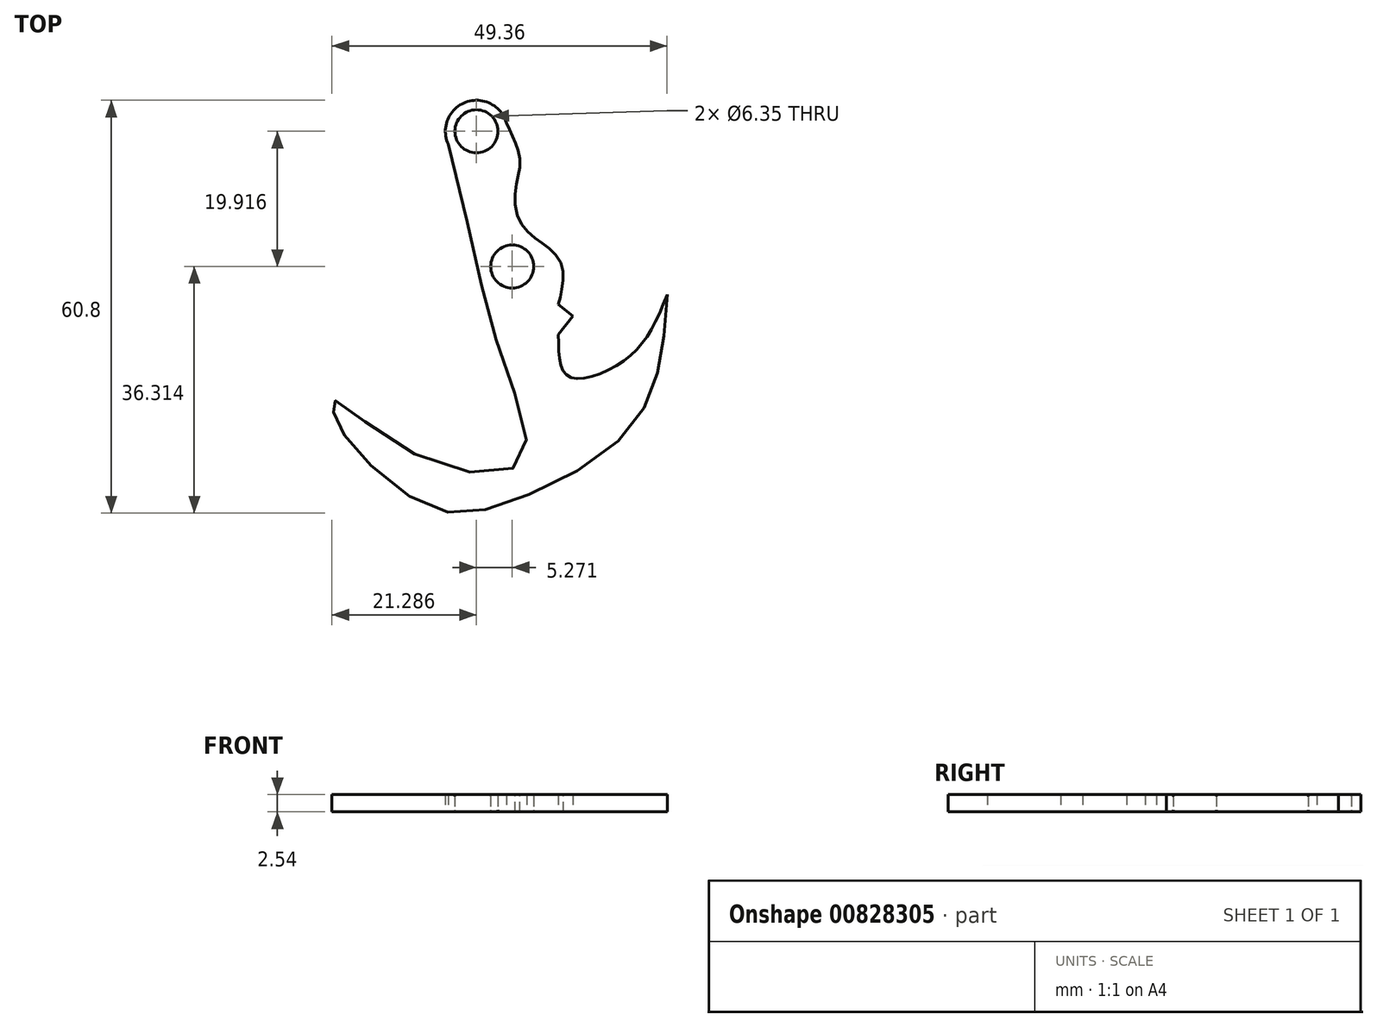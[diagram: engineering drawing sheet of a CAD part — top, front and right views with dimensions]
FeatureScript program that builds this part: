
annotation { "Feature Type Name" : "Feature", "Feature Type Description" : "" }
export const myFeature = defineFeature(function(context is Context, id is Id, definition is map)
    precondition{}
    {
        {
            var Q0;
            Q0=qCreatedBy(makeId("Top.planeOp"),FACE);
            var sketch = newSketch(context, id + "F0", { "sketchPlane" : qUnion([Q0])});
            skArc(sketch, "E0", {"start": v(-4, 46.8) * mm, "mid": v(-9.99, 49.84) * mm, "end": v(-12.56, 43.65) * mm});
            skCircle(sketch, "E1", {"center": v(-8.4, 45.55) * mm, "radius": 3.18 * mm});
            skFitSpline(sketch, "E2", {"points": [v(-12.56, 43.65) * mm, v(-4.64, 12.14) * mm, v(-1.72, -3.02) * mm, v(-16.97, -2.24) * mm, v(-29.51, 5.9) * mm, v(-29.51, 4.54) * mm, v(-27.31, 0) * mm, v(-15.32, -9.75) * mm, v(-4.5, -9.37) * mm, v(12.6, 0) * mm, v(18.23, 10) * mm, v(19.67, 21.48) * mm], "startDerivative": vector(76.44, -297.3) * mm, "endDerivative": vector(7.48, 151.48) * mm});
            skFitSpline(sketch, "E3", {"points": [v(19.67, 21.48) * mm, v(13.57, 11.94) * mm, v(5.22, 9.42) * mm, v(3.66, 15.63) * mm], "startDerivative": vector(-13.47, -34.19) * mm, "endDerivative": vector(-0.2, 29.03) * mm});
            skLineSegment(sketch, "E4", {"start": v(3.66, 15.63) * mm, "end": v(5.8, 18.35) * mm});
            skLineSegment(sketch, "E5", {"start": v(5.8, 18.35) * mm, "end": v(3.66, 20.03) * mm});
            skFitSpline(sketch, "E6", {"points": [v(-4, 46.8) * mm, v(-3.13, 44.86) * mm, v(-2.26, 42.72) * mm, v(-2.06, 40) * mm, v(-2.64, 37) * mm, v(-2.26, 32.82) * mm, v(0, 30) * mm, v(2.5, 28.16) * mm, v(4.25, 25.54) * mm, v(4.15, 22.33) * mm, v(3.66, 20.03) * mm], "startDerivative": vector(9.94, -22.66) * mm, "endDerivative": vector(-7.63, -25.15) * mm});
            skLineSegment(sketch, "E7", {"start": v(-2.64, 37) * mm, "end": v(-10.44, 34.97) * mm, "construction": true});
            skLineSegment(sketch, "E8", {"start": v(0, 30) * mm, "end": v(-8.86, 29.25) * mm, "construction": true});
            skCircle(sketch, "E9", {"center": v(-3.13, 25.63) * mm, "radius": 3.18 * mm});
            skSolve(sketch);
        }
        {
            var Q0;
            Q0 = qSketchRegion(id + "F0", true);
            extrude(context, id + "F1", {"entities" : qUnion([Q0]), "depth" : 2.54 * mm, "offsetDistance" : 25.4 * mm});
        }
        {
            var Q0;
            Q0=makeQuery(id+"F1.opExtrude","CAP_EDGE",EDGE,{"disambiguationData":[OSD([sQuery(id+"F0.wireOp",EDGE,"E1")])],"isStart":false});
            var Q1;
            Q1=makeQuery(id+"F1.opExtrude","CAP_EDGE",EDGE,{"disambiguationData":[OSD([sQuery(id+"F0.wireOp",EDGE,"E1")])],"isStart":true});
            var Q2;
            Q2=makeQuery(id+"F1.opExtrude","CAP_EDGE",EDGE,{"disambiguationData":[OSD([sQuery(id+"F0.wireOp",EDGE,"E9")])],"isStart":true});
            var Q3;
            Q3=makeQuery(id+"F1.opExtrude","CAP_EDGE",EDGE,{"disambiguationData":[OSD([sQuery(id+"F0.wireOp",EDGE,"E9")])],"isStart":false});
            fillet(context, id + "F2", {"entities" : qUnion([Q0, Q1, Q2, Q3]), "radius" : 0.25 * mm, "tangentPropagation" : true, "allowEdgeOverflow" : false});
        }
    });
